# Revit family: QF_MACOM_HOSF330A-2M
name_source: partatom
category: Specialty Equipment
units: mm (PartAtom-declared; Revit-internal decimal feet)

## family parameters
Always vertical = Yes
Cut with Voids When Loaded = No
OmniClass Number = 23.40.40.14.27
OmniClass Title = Ice Machines
Part Type = Normal
Room Calculation Point = No
Round Connector Dimension = Use Diameter
Shared = No
Work Plane-Based = No

## types (1)
- HOSF330A-2M
    BTUH = 3400,0 Btu/h
    Base Height = 152 mm
    Capacity = 36,00 kg
    Cold Water Connection Height = 109 mm
    Cold Water Flow = 0 m³/h
    Cold Water Maximum Pressure = 0,00 bar
    Cold Water Minimum Pressure = 0,00 bar
    Cold Water Size = 1"
    Cold Water Temperature Recommended = 0 °F
    Conn Conduit = Yes
    Cycle = 60 Hz
    Default Elevation = 0 mm
    Depth = 660 mm
    Description = MAQUINA DE GELO CUBELET HOSHIZAKI, PRODUCAO ATE 130KG/DIA, COM DEPOSITO 36KG - 220V MONOF - F-330BAJ-C-610X653X990
    Elec Conn Connection Height = 142 mm
    FL Amps = 7 A
    Height = 990 mm
    Indirect Waste Connection Height = 49 mm
    Indirect Waste Flow = 0 m³/h
    Indirect Waste Size = 1"
    Length = 610 mm
    Manufacturer = MACOM
    Max Overcurrent Protection = 0 A
    Min Ckt Ampacity = 0 A
    Model = HOSF330A-2M
    Phase = 1
    Refrigerant Type = R-404A
    URL = https://www.acosmacom.com.br
    Volts = 220 V
    Volume = 0,40 m³
    Watts = 628 W
    Weight = 67,00 kg

## geometry (parser evidence)
native form markers: Blend x6, Sweep x2
no freeform markers — native parametric forms only
